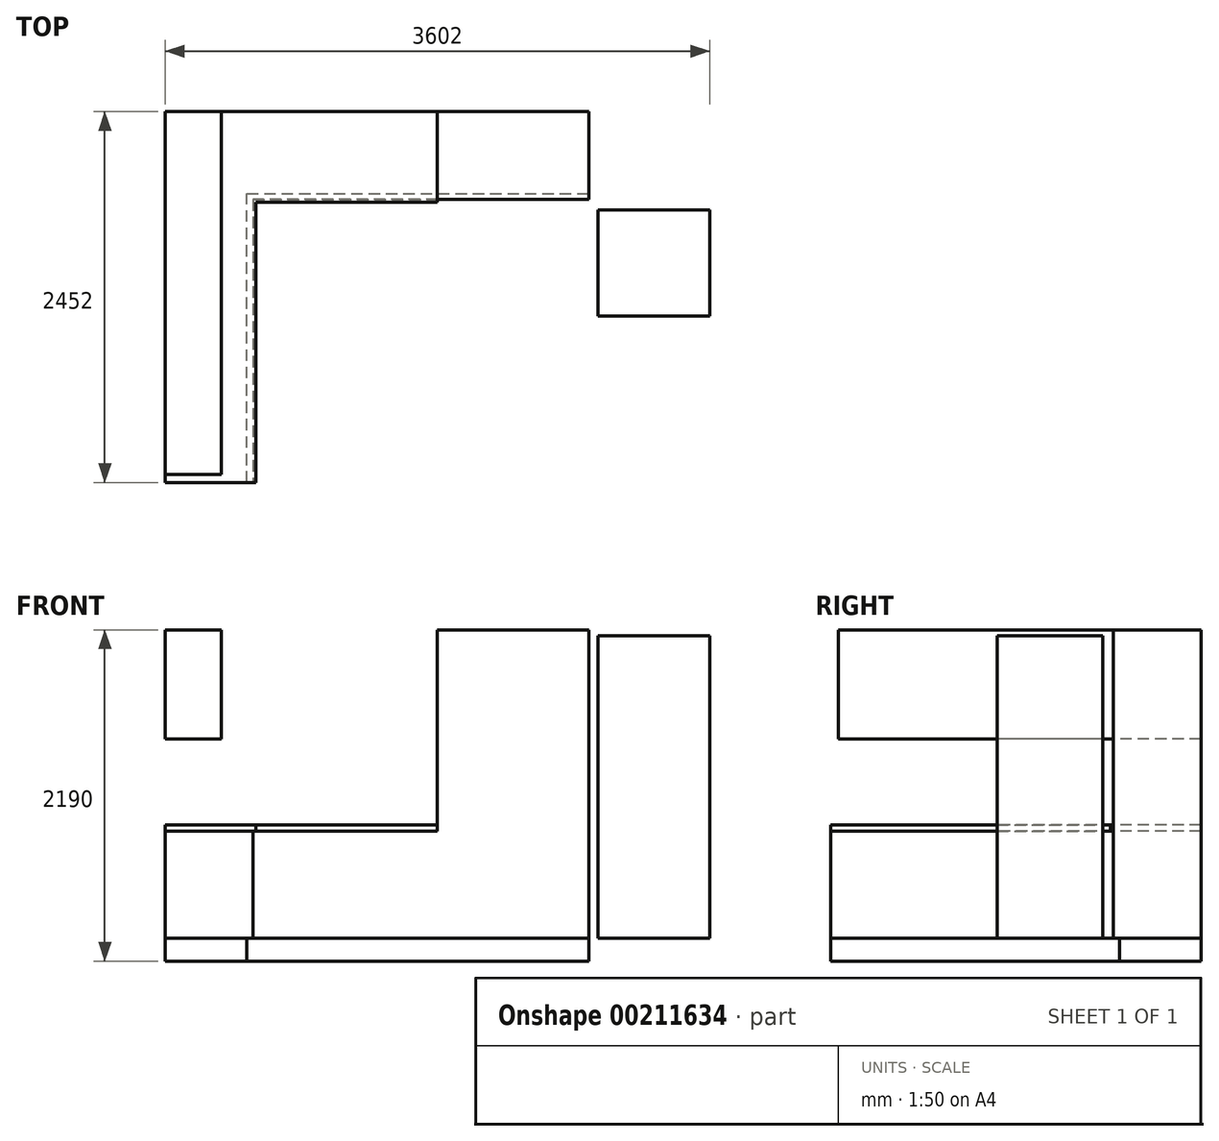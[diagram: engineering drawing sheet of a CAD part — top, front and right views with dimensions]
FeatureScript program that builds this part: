
annotation { "Feature Type Name" : "Feature", "Feature Type Description" : "" }
export const myFeature = defineFeature(function(context is Context, id is Id, definition is map)
    precondition{}
    {
        {
            var Q0;
            Q0=qCreatedBy(makeId("Top.planeOp"),FACE);
            var sketch = newSketch(context, id + "F0", { "sketchPlane" : qUnion([Q0])});
            skLineSegment(sketch, "E0.bottom", {"start": v(0, 0) * mm, "end": v(2825, 0) * mm});
            skLineSegment(sketch, "E0.top", {"start": v(0, -4000) * mm, "end": v(2825, -4000) * mm});
            skLineSegment(sketch, "E0.left", {"start": v(0, 0) * mm, "end": v(0, -4000) * mm});
            skLineSegment(sketch, "E0.right", {"start": v(2825, 0) * mm, "end": v(2825, -550) * mm});
            skLineSegment(sketch, "E1", {"start": v(0, -2452) * mm, "end": v(600, -2452) * mm});
            skLineSegment(sketch, "E2", {"start": v(600, -2452) * mm, "end": v(600, -600) * mm});
            skLineSegment(sketch, "E3", {"start": v(600, -600) * mm, "end": v(1800, -600) * mm});
            skLineSegment(sketch, "E4", {"start": v(2802, -580) * mm, "end": v(2802, 0) * mm});
            skLineSegment(sketch, "E5", {"start": v(1800, 0) * mm, "end": v(1800, -600) * mm});
            skLineSegment(sketch, "E6", {"start": v(1800, -580) * mm, "end": v(2802, -580) * mm});
            skLineSegment(sketch, "E7", {"start": v(2825, -550) * mm, "end": v(3622, -550) * mm});
            skLineSegment(sketch, "E8", {"start": v(3622, -550) * mm, "end": v(3622, -1400) * mm});
            skLineSegment(sketch, "E9", {"start": v(3622, -1400) * mm, "end": v(2825, -1400) * mm});
            skLineSegment(sketch, "E10", {"start": v(2825, -1400) * mm, "end": v(2825, -4000) * mm});
            skLineSegment(sketch, "E11.bottom", {"start": v(2862, -650) * mm, "end": v(3602, -650) * mm});
            skLineSegment(sketch, "E11.top", {"start": v(2862, -1350) * mm, "end": v(3602, -1350) * mm});
            skLineSegment(sketch, "E11.left", {"start": v(2862, -650) * mm, "end": v(2862, -1350) * mm});
            skLineSegment(sketch, "E11.right", {"start": v(3602, -650) * mm, "end": v(3602, -1350) * mm});
            skLineSegment(sketch, "E12", {"start": v(1800, -580) * mm, "end": v(580, -580) * mm});
            skLineSegment(sketch, "E13", {"start": v(580, -580) * mm, "end": v(580, -2452) * mm});
            skLineSegment(sketch, "E14", {"start": v(2825, -550) * mm, "end": v(2825, -1400) * mm});
            skLineSegment(sketch, "E15", {"start": v(3022, -550) * mm, "end": v(3022, -650) * mm});
            skLineSegment(sketch, "E16", {"start": v(3022, -1350) * mm, "end": v(3022, -1400) * mm});
            skLineSegment(sketch, "E17", {"start": v(540, -2452) * mm, "end": v(540, -540) * mm});
            skLineSegment(sketch, "E18", {"start": v(540, -540) * mm, "end": v(2802, -540) * mm});
            skLineSegment(sketch, "E19", {"start": v(370, 0) * mm, "end": v(370, -2400) * mm});
            skLineSegment(sketch, "E20", {"start": v(370, -2400) * mm, "end": v(0, -2400) * mm});
            skSolve(sketch);
        }
        {
            var Q0;
            {var subQ0=sQuery(id+"F0.wireOp",EDGE,"E4");Q0=makeQuery(id+"F0.imprint","IMPRINT",FACE,{"disambiguationData":[TD([[makeQuery(id+"F0.imprint","IMPRINT",EDGE,{"derivedFrom":subQ0}),1.0]])]});}
            extrude(context, id + "F1", {"entities" : qUnion([Q0]), "depth" : 2190 * mm, "hasSecondDirection" : true, "secondDirectionOppositeDirection" : false, "secondDirectionDepth" : 150 * mm});
        }
        {
            var Q0;
            {var subQ3=sQuery(id+"F0.wireOp",EDGE,"E12");Q0=makeQuery(id+"F0.imprint","IMPRINT",FACE,{"disambiguationData":[TD([[makeQuery(id+"F0.imprint","IMPRINT",EDGE,{"derivedFrom":subQ3}),-1.0]])]});}
            var Q1;
            {var subQ8=sQuery(id+"F0.wireOp",EDGE,"E17");Q1=makeQuery(id+"F0.imprint","IMPRINT",FACE,{"disambiguationData":[TD([[makeQuery(id+"F0.imprint","IMPRINT",EDGE,{"derivedFrom":subQ8}),1.0]])]});}
            var Q2;
            {var subQ3=sQuery(id+"F0.wireOp",EDGE,"E19");Q2=makeQuery(id+"F0.imprint","IMPRINT",FACE,{"disambiguationData":[TD([[makeQuery(id+"F0.imprint","IMPRINT",EDGE,{"derivedFrom":subQ3}),-1.0]])]});}
            extrude(context, id + "F2", {"entities" : qUnion([Q0, Q1, Q2]), "operationType" : NewBodyOperationType.ADD, "depth" : 860 * mm, "hasSecondDirection" : true, "secondDirectionOppositeDirection" : false, "secondDirectionDepth" : 150 * mm});
        }
        {
            var Q0;
            {var subQ3=sQuery(id+"F0.wireOp",EDGE,"E12");Q0=makeQuery(id+"F0.imprint","IMPRINT",FACE,{"disambiguationData":[TD([[makeQuery(id+"F0.imprint","IMPRINT",EDGE,{"derivedFrom":subQ3}),-1.0]])]});}
            var Q1;
            {var subQ3=sQuery(id+"F0.wireOp",EDGE,"E2");Q1=makeQuery(id+"F0.imprint","IMPRINT",FACE,{"disambiguationData":[TD([[makeQuery(id+"F0.imprint","IMPRINT",EDGE,{"derivedFrom":subQ3}),1.0]])]});}
            var Q2;
            {var subQ8=sQuery(id+"F0.wireOp",EDGE,"E17");Q2=makeQuery(id+"F0.imprint","IMPRINT",FACE,{"disambiguationData":[TD([[makeQuery(id+"F0.imprint","IMPRINT",EDGE,{"derivedFrom":subQ8}),1.0]])]});}
            var Q3;
            {var subQ3=sQuery(id+"F0.wireOp",EDGE,"E19");Q3=makeQuery(id+"F0.imprint","IMPRINT",FACE,{"disambiguationData":[TD([[makeQuery(id+"F0.imprint","IMPRINT",EDGE,{"derivedFrom":subQ3}),-1.0]])]});}
            var Q4;
            Q4=makeQuery(id+"F2.opExtrude","CAP_FACE",FACE,{"disambiguationData":[OSD([sQuery(id+"F0.wireOp",EDGE,"E0.bottom"),sQuery(id+"F0.wireOp",EDGE,"E0.left"),sQuery(id+"F0.wireOp",EDGE,"E1"),sQuery(id+"F0.wireOp",EDGE,"E5"),sQuery(id+"F0.wireOp",EDGE,"E12"),sQuery(id+"F0.wireOp",EDGE,"E13")])],"isStart":false});
            var Q5;
            Q5=makeQuery(id+"F2.opExtrude","CAP_FACE",FACE,{"disambiguationData":[OSD([sQuery(id+"F0.wireOp",EDGE,"E0.bottom"),sQuery(id+"F0.wireOp",EDGE,"E0.left"),sQuery(id+"F0.wireOp",EDGE,"E1"),sQuery(id+"F0.wireOp",EDGE,"E5"),sQuery(id+"F0.wireOp",EDGE,"E12"),sQuery(id+"F0.wireOp",EDGE,"E13")])],"isStart":false});
            extrude(context, id + "F3", {"entities" : qUnion([Q0, Q1, Q2, Q3]), "endBoundEntityFace" : qUnion([Q4]), "depth" : 900 * mm, "hasSecondDirection" : true, "secondDirectionBound" : BoundingType.UP_TO_SURFACE, "secondDirectionOppositeDirection" : false, "secondDirectionBoundEntityFace" : qUnion([Q5]), "secondDirectionDepth" : 931 * mm});
        }
        {
            var Q0;
            {var subQ8=sQuery(id+"F0.wireOp",EDGE,"E17");Q0=makeQuery(id+"F0.imprint","IMPRINT",FACE,{"disambiguationData":[TD([[makeQuery(id+"F0.imprint","IMPRINT",EDGE,{"derivedFrom":subQ8}),1.0]])]});}
            var Q1;
            {var subQ0=sQuery(id+"F0.wireOp",EDGE,"E4");var subQ1=sQuery(id+"F0.wireOp",EDGE,"E0.bottom");var subQ2=makeQuery(id+"F0.imprint","INTERSECT",VERTEX,{"derivedFrom":[subQ1,subQ0]});Q1=makeQuery(id+"F0.imprint","IMPRINT",FACE,{"disambiguationData":[TD([[makeQuery(id+"F0.imprint","IMPRINT",EDGE,{"disambiguationData":[TD([[subQ2,1.0]])],"derivedFrom":subQ1}),-1.0]])]});}
            var Q2;
            {var subQ3=sQuery(id+"F0.wireOp",EDGE,"E19");Q2=makeQuery(id+"F0.imprint","IMPRINT",FACE,{"disambiguationData":[TD([[makeQuery(id+"F0.imprint","IMPRINT",EDGE,{"derivedFrom":subQ3}),-1.0]])]});}
            extrude(context, id + "F4", {"entities" : qUnion([Q0, Q1, Q2]), "endBound" : BoundingType.UP_TO_NEXT, "depth" : 25 * mm});
        }
        {
            var Q0;
            {var subQ3=sQuery(id+"F0.wireOp",EDGE,"E11.left");Q0=makeQuery(id+"F0.imprint","IMPRINT",FACE,{"disambiguationData":[TD([[makeQuery(id+"F0.imprint","IMPRINT",EDGE,{"derivedFrom":subQ3}),1.0]])]});}
            extrude(context, id + "F5", {"entities" : qUnion([Q0]), "depth" : 2150 * mm, "hasSecondDirection" : true, "secondDirectionOppositeDirection" : false, "secondDirectionDepth" : 150 * mm});
        }
        {
            var Q0;
            {var subQ3=sQuery(id+"F0.wireOp",EDGE,"E19");Q0=makeQuery(id+"F0.imprint","IMPRINT",FACE,{"disambiguationData":[TD([[makeQuery(id+"F0.imprint","IMPRINT",EDGE,{"derivedFrom":subQ3}),-1.0]])]});}
            extrude(context, id + "F6", {"entities" : qUnion([Q0]), "depth" : (910 + 560 + 720) * mm, "hasSecondDirection" : true, "secondDirectionOppositeDirection" : false, "secondDirectionDepth" : (910 + 560) * mm});
        }
    });
